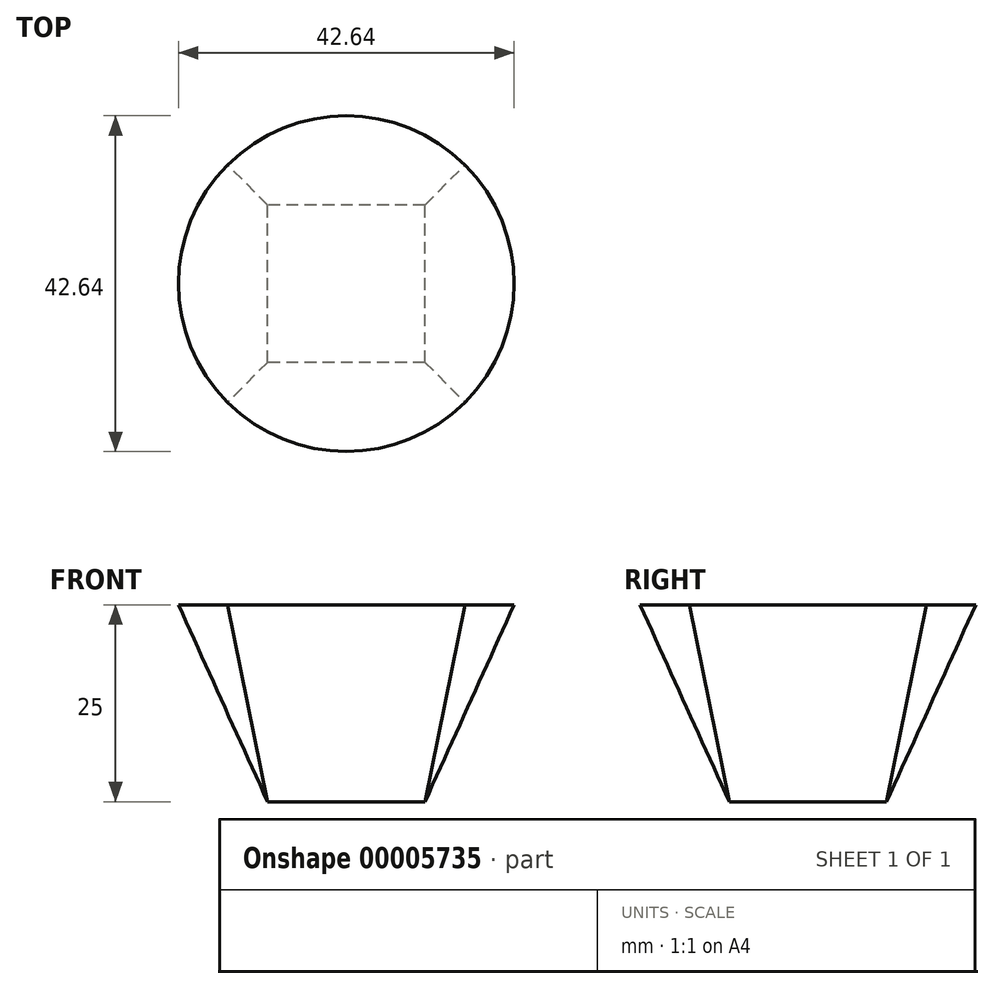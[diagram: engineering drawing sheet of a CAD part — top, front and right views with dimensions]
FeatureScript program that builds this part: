
annotation { "Feature Type Name" : "Feature", "Feature Type Description" : "" }
export const myFeature = defineFeature(function(context is Context, id is Id, definition is map)
    precondition{}
    {
        {
            var Q0;
            Q0=qCreatedBy(makeId("Top.planeOp"),FACE);
            var sketch = newSketch(context, id + "F0", { "sketchPlane" : qUnion([Q0])});
            skLineSegment(sketch, "E0.bottom", {"start": v(10, -10) * mm, "end": v(-10, -10) * mm});
            skLineSegment(sketch, "E0.top", {"start": v(10, 10) * mm, "end": v(-10, 10) * mm});
            skLineSegment(sketch, "E0.left", {"start": v(10, -10) * mm, "end": v(10, 10) * mm});
            skLineSegment(sketch, "E0.right", {"start": v(-10, -10) * mm, "end": v(-10, 10) * mm});
            skPoint(sketch, "E0.middle", {"position": v(0, 0) * mm});
            skSolve(sketch);
        }
        {
            var Q0;
            Q0=qCreatedBy(makeId("Top.planeOp"),FACE);
            cPlane(context, id + "F1", {"entities" : qUnion([Q0]), "cplaneType" : CPlaneType.OFFSET, "offset" : 25 * mm, "width" : 150 * mm, "height" : 150 * mm});
        }
        {
            var Q0;
            Q0=qCreatedBy(id+"F1.planeOp",FACE);
            var sketch = newSketch(context, id + "F2", { "sketchPlane" : qUnion([Q0])});
            skCircle(sketch, "E1", {"center": v(0, 0) * mm, "radius": 21.32 * mm});
            skSolve(sketch);
        }
        {
            var Q0;
            Q0=makeQuery(id+"F0.imprint","IMPRINT",FACE,{"disambiguationData":[TD([[makeQuery(id+"F0.imprint","IMPRINT",EDGE,{"derivedFrom":sQuery(id+"F0.wireOp",EDGE,"E0.bottom")}),-1.0]])]});
            var Q1;
            Q1=makeQuery(id+"F2.imprint","IMPRINT",FACE,{"disambiguationData":[TD([[makeQuery(id+"F2.imprint","IMPRINT",EDGE,{"derivedFrom":sQuery(id+"F2.wireOp",EDGE,"E1")}),1.0]])]});
            loft(context, id + "F3", {"sheetProfilesArray" : [{ "sheetProfileEntities" : qUnion([Q0]) }, { "sheetProfileEntities" : qUnion([Q1]) }]});
        }
    });
